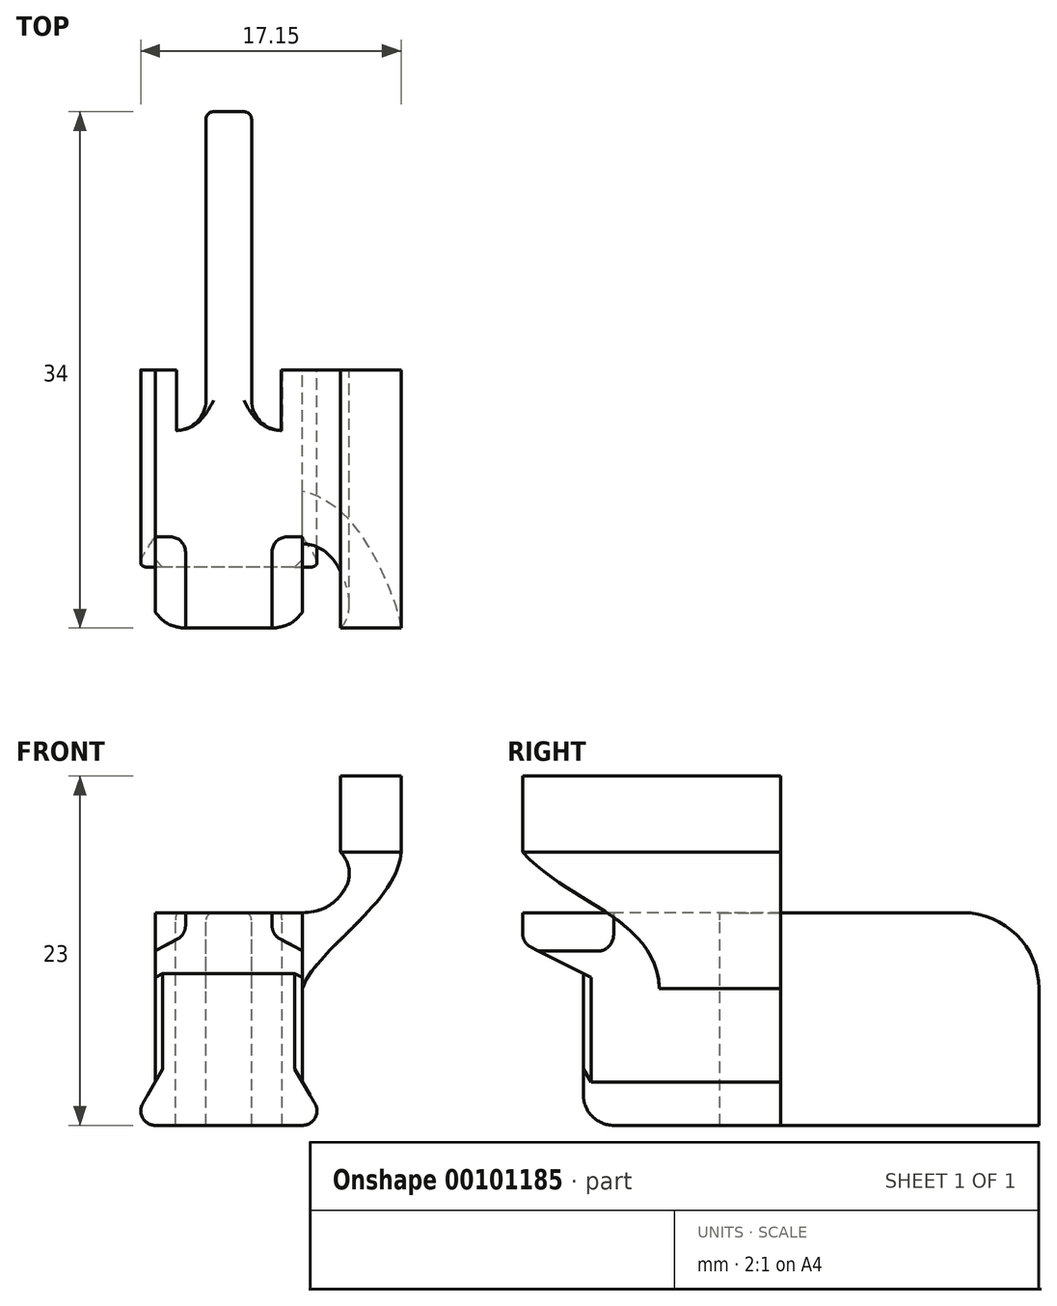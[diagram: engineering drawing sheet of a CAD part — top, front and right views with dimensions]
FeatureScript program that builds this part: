
annotation { "Feature Type Name" : "Feature", "Feature Type Description" : "" }
export const myFeature = defineFeature(function(context is Context, id is Id, definition is map)
    precondition{}
    {
        {
            var Q0;
            Q0=qCreatedBy(makeId("Top.planeOp"),FACE);
            var sketch = newSketch(context, id + "F0", { "sketchPlane" : qUnion([Q0])});
            skLineSegment(sketch, "E0.bottom", {"start": v(4.85, 4.5) * mm, "end": v(-4.85, 4.5) * mm});
            skLineSegment(sketch, "E0.top", {"start": v(4.85, -4.5) * mm, "end": v(-4.85, -4.5) * mm});
            skLineSegment(sketch, "E0.left", {"start": v(4.85, 4.5) * mm, "end": v(4.85, -4.5) * mm});
            skLineSegment(sketch, "E0.right", {"start": v(-4.85, 4.5) * mm, "end": v(-4.85, -4.5) * mm});
            skPoint(sketch, "E0.middle", {"position": v(0, 0) * mm});
            skSolve(sketch);
        }
        {
            var Q0;
            Q0 = qSketchRegion(id + "F0", true);
            extrude(context, id + "F1", {"entities" : qUnion([Q0]), "depth" : 10 * mm});
        }
        {
            var Q0;
            {var subQ0=sQuery(id+"F5.wireOp",EDGE,"E6.right");var subQ1=sQuery(id+"F0.wireOp",EDGE,"E0.bottom");Q0=makeQuery(id+"F8.boolean.opBoolean","MERGE",FACE,{"derivedFrom":[makeQuery(id+"F6.boolean.opBoolean","MERGE",FACE,{"derivedFrom":[makeQuery(id+"F1.opExtrude","SWEPT_FACE",FACE,{"disambiguationData":[OSD([subQ1])]}),makeQuery(id+"F6.opExtrude","SWEPT_FACE",FACE,{"disambiguationData":[OSD([subQ0])]})]}),makeQuery(id+"F8.opExtrude","CAP_FACE",FACE,{"disambiguationData":[OSD([subQ1,sQuery(id+"F0.wireOp",EDGE,"E0.left"),subQ0,sQuery(id+"F7.wireOp",EDGE,"E10.bottom"),sQuery(id+"F7.wireOp",EDGE,"E10.left"),sQuery(id+"F7.wireOp",EDGE,"E10.right"),sQuery(id+"F7.wireOp",EDGE,"E11"),sQuery(id+"F7.wireOp",EDGE,"E12"),sQuery(id+"F7.wireOp",EDGE,"E13.bottom"),sQuery(id+"F7.wireOp",EDGE,"E13.right"),sQuery(id+"F7.wireOp",EDGE,"lhwnHaxV-OdRf-uXD5-QTkz-yTmSrOFCT4aj")])],"isStart":true})]});}
            var sketch = newSketch(context, id + "F2", { "sketchPlane" : qUnion([Q0])});
            skCircle(sketch, "E1", {"center": v(-4.85, 0.95) * mm, "radius": 0.95 * mm});
            skLineSegment(sketch, "E2", {"start": v(-4.85, 2.85) * mm, "end": v(-5.67, 1.42) * mm});
            skLineSegment(sketch, "E3", {"start": v(0, 0) * mm, "end": v(0, 3.09) * mm, "construction": true});
            skCircle(sketch, "E4", {"center": v(4.85, 0.95) * mm, "radius": 0.95 * mm});
            skLineSegment(sketch, "E5", {"start": v(4.85, 2.85) * mm, "end": v(5.67, 1.43) * mm});
            skSolve(sketch);
        }
        {
            var Q0;
            Q0 = qSketchRegion(id + "F2", true);
            var Q1;
            {var subQ0=sQuery(id+"F2.wireOp",EDGE,"E2");Q1=makeQuery(id+"F2.imprint","IMPRINT",FACE,{"disambiguationData":[TD([[makeQuery(id+"F2.imprint","IMPRINT",EDGE,{"derivedFrom":subQ0}),1.0]])]});}
            var Q2;
            {var subQ0=sQuery(id+"F2.wireOp",EDGE,"E5");Q2=makeQuery(id+"F2.imprint","IMPRINT",FACE,{"disambiguationData":[TD([[makeQuery(id+"F2.imprint","IMPRINT",EDGE,{"derivedFrom":subQ0}),-1.0]])]});}
            var Q3;
            Q3=makeQuery(id+"F1.opExtrude","SWEPT_FACE",FACE,{"disambiguationData":[OSD([sQuery(id+"F0.wireOp",EDGE,"E0.top")])]});
            extrude(context, id + "F3", {"entities" : qUnion([Q0, Q1, Q2]), "operationType" : NewBodyOperationType.ADD, "endBound" : BoundingType.UP_TO_SURFACE, "oppositeDirection" : true, "endBoundEntityFace" : qUnion([Q3]), "depth" : 25 * mm});
        }
        {
            var Q0;
            Q0=makeQuery(id+"F1.opExtrude","CAP_EDGE",EDGE,{"disambiguationData":[OSD([sQuery(id+"F0.wireOp",EDGE,"E0.top")])],"isStart":true});
            fillet(context, id + "F4", {"entities" : qUnion([Q0]), "radius" : 2 * mm, "allowEdgeOverflow" : false});
        }
        {
            var Q0;
            Q0=makeQuery(id+"F1.opExtrude","SWEPT_FACE",FACE,{"disambiguationData":[OSD([sQuery(id+"F0.wireOp",EDGE,"E0.left")])]});
            var sketch = newSketch(context, id + "F5", { "sketchPlane" : qUnion([Q0])});
            skLineSegment(sketch, "E6.bottom", {"start": v(-4.5, 10) * mm, "end": v(4.5, 10) * mm});
            skLineSegment(sketch, "E6.top", {"start": v(-4.5, 14) * mm, "end": v(4.5, 14) * mm});
            skLineSegment(sketch, "E6.left", {"start": v(-4.5, 10) * mm, "end": v(-4.5, 14) * mm});
            skLineSegment(sketch, "E6.right", {"start": v(4.5, 10) * mm, "end": v(4.5, 14) * mm});
            skLineSegment(sketch, "E7", {"start": v(-4.5, 14) * mm, "end": v(-8.5, 14) * mm});
            skLineSegment(sketch, "E8", {"start": v(-8.5, 14) * mm, "end": v(-8.5, 12) * mm});
            skLineSegment(sketch, "E9", {"start": v(-8.5, 12) * mm, "end": v(-4.5, 10) * mm});
            skSolve(sketch);
        }
        {
            var Q0;
            Q0 = qSketchRegion(id + "F5", true);
            var Q1;
            Q1=makeQuery(id+"F1.opExtrude","SWEPT_FACE",FACE,{"disambiguationData":[OSD([sQuery(id+"F0.wireOp",EDGE,"E0.right")])]});
            extrude(context, id + "F6", {"entities" : qUnion([Q0]), "operationType" : NewBodyOperationType.ADD, "endBound" : BoundingType.UP_TO_SURFACE, "oppositeDirection" : true, "endBoundEntityFace" : qUnion([Q1]), "offsetDistance" : 25 * mm, "depth" : 25 * mm});
        }
        {
            var Q0;
            {var subQ0=sQuery(id+"F0.wireOp",EDGE,"E0.bottom");Q0=makeQuery(id+"F6.boolean.opBoolean","MERGE",FACE,{"derivedFrom":[makeQuery(id+"F3.boolean.opBoolean","MERGE",FACE,{"derivedFrom":[makeQuery(id+"F1.opExtrude","SWEPT_FACE",FACE,{"disambiguationData":[OSD([subQ0])]}),makeQuery(id+"F3.opExtrude","CAP_FACE",FACE,{"disambiguationData":[OSD([subQ0,sQuery(id+"F0.wireOp",EDGE,"E0.left"),sQuery(id+"F2.wireOp",EDGE,"E1"),sQuery(id+"F2.wireOp",EDGE,"E2")])],"isStart":true}),makeQuery(id+"F3.opExtrude","CAP_FACE",FACE,{"disambiguationData":[OSD([subQ0,sQuery(id+"F0.wireOp",EDGE,"E0.right"),sQuery(id+"F2.wireOp",EDGE,"E4"),sQuery(id+"F2.wireOp",EDGE,"E5")])],"isStart":true})]}),makeQuery(id+"F6.opExtrude","SWEPT_FACE",FACE,{"disambiguationData":[OSD([sQuery(id+"F5.wireOp",EDGE,"E6.right")])]})]});}
            var sketch = newSketch(context, id + "F7", { "sketchPlane" : qUnion([Q0])});
            skLineSegment(sketch, "E10.bottom", {"start": v(-8.35, 23) * mm, "end": v(-11.35, 23) * mm});
            skLineSegment(sketch, "E10.right", {"start": v(-11.35, 23) * mm, "end": v(-11.35, 18) * mm});
            skFitSpline(sketch, "E11", {"points": [v(-8.35, 18) * mm, v(-4.85, 14) * mm], "startDerivative": vector(0.6, -7.03) * mm, "endDerivative": vector(6.53, -0.05) * mm});
            skFitSpline(sketch, "E12", {"points": [v(-11.35, 18) * mm, v(-4.85, 9) * mm], "startDerivative": vector(0.57, -10.14) * mm, "endDerivative": vector(2.5, -7.8) * mm});
            skLineSegment(sketch, "E13.bottom", {"start": v(-8.35, 23) * mm, "end": v(-7.35, 23) * mm});
            skLineSegment(sketch, "E13.top", {"start": v(-8.35, 18) * mm, "end": v(-7.35, 18) * mm});
            skLineSegment(sketch, "E13.right", {"start": v(-7.35, 23) * mm, "end": v(-7.35, 18) * mm});
            skLineSegment(sketch, "E14", {"start": v(-4.85, 9) * mm, "end": v(-4.85, 14) * mm});
            skSolve(sketch);
        }
        {
            var Q0;
            Q0 = qSketchRegion(id + "F7", true);
            var Q1;
            Q1=makeQuery(id+"F6.opExtrude","SWEPT_FACE",FACE,{"disambiguationData":[OSD([sQuery(id+"F5.wireOp",EDGE,"E8")])]});
            extrude(context, id + "F8", {"entities" : qUnion([Q0]), "operationType" : NewBodyOperationType.ADD, "endBound" : BoundingType.UP_TO_SURFACE, "oppositeDirection" : true, "endBoundEntityFace" : qUnion([Q1]), "offsetDistance" : 25 * mm, "depth" : 25 * mm});
        }
        {
            var Q0;
            Q0=makeQuery(id+"F8.opExtrude","SWEPT_FACE",FACE,{"disambiguationData":[OSD([sQuery(id+"F7.wireOp",EDGE,"E10.right")])]});
            var sketch = newSketch(context, id + "F9", { "sketchPlane" : qUnion([Q0])});
            skFitSpline(sketch, "E15", {"points": [v(-8.5, 18) * mm, v(0.5, 9) * mm], "startDerivative": vector(8.93, -10.15) * mm, "endDerivative": vector(0.55, -14.12) * mm});
            skLineSegment(sketch, "E16", {"start": v(-8.5, 18) * mm, "end": v(-8.86, 18) * mm});
            skLineSegment(sketch, "E17", {"start": v(-8.86, 18) * mm, "end": v(-8.86, 9) * mm});
            skLineSegment(sketch, "E18", {"start": v(-8.86, 9) * mm, "end": v(0.5, 9) * mm});
            skSolve(sketch);
        }
        {
            var Q0;
            Q0 = qSketchRegion(id + "F9", true);
            var Q1;
            Q1=makeQuery(id+"F6.boolean.opBoolean","MERGE",FACE,{"derivedFrom":[makeQuery(id+"F1.opExtrude","SWEPT_FACE",FACE,{"disambiguationData":[OSD([sQuery(id+"F0.wireOp",EDGE,"E0.left")])]}),makeQuery(id+"F6.opExtrude","CAP_FACE",FACE,{"disambiguationData":[OSD([sQuery(id+"F5.wireOp",EDGE,"E6.bottom"),sQuery(id+"F5.wireOp",EDGE,"E6.top"),sQuery(id+"F5.wireOp",EDGE,"E6.right"),sQuery(id+"F5.wireOp",EDGE,"E7"),sQuery(id+"F5.wireOp",EDGE,"E8"),sQuery(id+"F5.wireOp",EDGE,"E9")])],"isStart":true})]});
            extrude(context, id + "F10", {"entities" : qUnion([Q0]), "operationType" : NewBodyOperationType.REMOVE, "endBound" : BoundingType.UP_TO_SURFACE, "oppositeDirection" : true, "endBoundEntityFace" : qUnion([Q1]), "depth" : 25 * mm});
        }
        {
            var Q0;
            Q0=qCreatedBy(makeId("Right.planeOp"),FACE);
            var sketch = newSketch(context, id + "F11", { "sketchPlane" : qUnion([Q0])});
            skLineSegment(sketch, "E19.bottom", {"start": v(3.5, 0) * mm, "end": v(25.5, 0) * mm});
            skLineSegment(sketch, "E19.top", {"start": v(3.5, 14) * mm, "end": v(25.5, 14) * mm});
            skLineSegment(sketch, "E19.left", {"start": v(3.5, 0) * mm, "end": v(3.5, 14) * mm});
            skLineSegment(sketch, "E19.right", {"start": v(25.5, 0) * mm, "end": v(25.5, 14) * mm});
            skSolve(sketch);
        }
        {
            var Q0;
            Q0 = qSketchRegion(id + "F11", true);
            extrude(context, id + "F12", {"entities" : qUnion([Q0]), "operationType" : NewBodyOperationType.ADD, "endBound" : BoundingType.SYMMETRIC, "depth" : 3 * mm});
        }
        {
            var Q0;
            Q0=makeQuery(id+"F12.opExtrude","SWEPT_EDGE",EDGE,{"disambiguationData":[OSD([sQuery(id+"F11.wireOp",EDGE,"E19.top"),sQuery(id+"F11.wireOp",EDGE,"E19.right")])]});
            fillet(context, id + "F13", {"entities" : qUnion([Q0]), "radius" : 5 * mm, "tangentPropagation" : true, "allowEdgeOverflow" : false});
        }
        {
            var Q0;
            Q0=makeQuery(id+"F1.opExtrude","SWEPT_EDGE",EDGE,{"disambiguationData":[OSD([sQuery(id+"F0.wireOp",EDGE,"E0.top"),sQuery(id+"F0.wireOp",EDGE,"E0.left")])]});
            var Q1;
            Q1=makeQuery(id+"F1.opExtrude","SWEPT_EDGE",EDGE,{"disambiguationData":[OSD([sQuery(id+"F0.wireOp",EDGE,"E0.top"),sQuery(id+"F0.wireOp",EDGE,"E0.right")])]});
            chamfer(context, id + "F14", {"entities" : qUnion([Q0, Q1]), "width" : 0.5 * mm});
        }
        {
            var Q0;
            {var subQ0=sQuery(id+"F11.wireOp",EDGE,"E19.right");var subQ1=sQuery(id+"F11.wireOp",EDGE,"E19.top");Q0=makeQuery(id+"F13.opFillet","BLEND_EDGE",EDGE,{"blendedFrom":[makeQuery(id+"F12.opExtrude","SWEPT_EDGE",EDGE,{"disambiguationData":[OSD([subQ1,subQ0])]}),makeQuery(id+"F12.opExtrude","CAP_FACE",FACE,{"disambiguationData":[OSD([sQuery(id+"F11.wireOp",EDGE,"E19.bottom"),subQ1,sQuery(id+"F11.wireOp",EDGE,"E19.left"),subQ0])],"isStart":false})],"blendedInto":[makeQuery(id+"F12.opExtrude","CAP_FACE",FACE,{"disambiguationData":[OSD([sQuery(id+"F11.wireOp",EDGE,"E19.bottom"),subQ1,sQuery(id+"F11.wireOp",EDGE,"E19.left"),subQ0])],"isStart":false})]});}
            var Q1;
            {var subQ0=sQuery(id+"F11.wireOp",EDGE,"E19.right");var subQ1=sQuery(id+"F11.wireOp",EDGE,"E19.top");Q1=makeQuery(id+"F13.opFillet","BLEND_EDGE",EDGE,{"blendedFrom":[makeQuery(id+"F12.opExtrude","SWEPT_EDGE",EDGE,{"disambiguationData":[OSD([subQ1,subQ0])]}),makeQuery(id+"F12.opExtrude","CAP_FACE",FACE,{"disambiguationData":[OSD([sQuery(id+"F11.wireOp",EDGE,"E19.bottom"),subQ1,sQuery(id+"F11.wireOp",EDGE,"E19.left"),subQ0])],"isStart":true})],"blendedInto":[makeQuery(id+"F12.opExtrude","CAP_FACE",FACE,{"disambiguationData":[OSD([sQuery(id+"F11.wireOp",EDGE,"E19.bottom"),subQ1,sQuery(id+"F11.wireOp",EDGE,"E19.left"),subQ0])],"isStart":true})]});}
            fillet(context, id + "F15", {"entities" : qUnion([Q0, Q1]), "radius" : 0.5 * mm, "tangentPropagation" : true, "allowEdgeOverflow" : false});
        }
        {
            var Q0;
            Q0=makeQuery(id+"F12.opExtrude","CAP_FACE",FACE,{"disambiguationData":[OSD([sQuery(id+"F11.wireOp",EDGE,"E19.bottom"),sQuery(id+"F11.wireOp",EDGE,"E19.top"),sQuery(id+"F11.wireOp",EDGE,"E19.left"),sQuery(id+"F11.wireOp",EDGE,"E19.right")])],"isStart":false});
            var sketch = newSketch(context, id + "F16", { "sketchPlane" : qUnion([Q0])});
            skText(sketch, "E20", { "text": "Renishaw", "fontName": "OpenSans-Bold.ttf"});
            const initialGuessF16  = {"E20": [0.00663, 0.00758, 1, 0, 0.00224]};
            skSetInitialGuess(sketch, initialGuessF16);
            skSolve(sketch);
        }
        {
            var Q0;
            {var subQ2=sQuery(id+"F5.wireOp",EDGE,"E8");var subQ7=sQuery(id+"F0.wireOp",EDGE,"E0.left");Q0=makeQuery(id+"F10.boolean.opBoolean","SPLIT",FACE,{"disambiguationData":[TD([makeQuery(id+"F1.opExtrude","SWEPT_FACE",FACE,{"disambiguationData":[OSD([subQ7])]})])],"derivedFrom":makeQuery(id+"F8.boolean.opBoolean","MERGE",FACE,{"derivedFrom":[makeQuery(id+"F6.opExtrude","SWEPT_FACE",FACE,{"disambiguationData":[OSD([subQ2])]}),makeQuery(id+"F8.opExtrude","CAP_FACE",FACE,{"disambiguationData":[OSD([subQ2])],"isStart":false})]})});}
            var sketch = newSketch(context, id + "F17", { "sketchPlane" : qUnion([Q0])});
            skLineSegment(sketch, "E21", {"start": v(-4.85, 14) * mm, "end": v(-2.85, 14) * mm});
            skLineSegment(sketch, "E22", {"start": v(-2.85, 14) * mm, "end": v(-2.85, 12.54) * mm});
            skLineSegment(sketch, "E23", {"start": v(-2.85, 12.54) * mm, "end": v(-4.85, 11.48) * mm});
            skLineSegment(sketch, "E24", {"start": v(-4.85, 11.48) * mm, "end": v(-4.85, 14) * mm});
            skLineSegment(sketch, "E25.MirrorCS", {"start": v(2.85, 14) * mm, "end": v(2.85, 12.54) * mm});
            skLineSegment(sketch, "E26.MirrorCS", {"start": v(4.85, 14) * mm, "end": v(2.85, 14) * mm});
            skLineSegment(sketch, "E27.MirrorCS", {"start": v(4.85, 11.48) * mm, "end": v(4.85, 14) * mm});
            skLineSegment(sketch, "E28.MirrorCS", {"start": v(2.85, 12.54) * mm, "end": v(4.85, 11.48) * mm});
            skSolve(sketch);
        }
        {
            var Q0;
            Q0 = qSketchRegion(id + "F17", true);
            extrude(context, id + "F18", {"entities" : qUnion([Q0]), "operationType" : NewBodyOperationType.REMOVE, "oppositeDirection" : true, "depth" : 6 * mm, "offsetDistance" : 25 * mm});
        }
        {
            var Q0;
            Q0=makeQuery(id+"F18.boolean.opBoolean","COPY",EDGE,{"derivedFrom":makeQuery(id+"F18.opExtrude","SWEPT_EDGE",EDGE,{"disambiguationData":[OSD([sQuery(id+"F17.wireOp",EDGE,"E25.MirrorCS"),sQuery(id+"F17.wireOp",EDGE,"E28.MirrorCS")])]})});
            var Q1;
            Q1=makeQuery(id+"F18.boolean.opBoolean","COPY",EDGE,{"derivedFrom":makeQuery(id+"F18.opExtrude","SWEPT_EDGE",EDGE,{"disambiguationData":[OSD([sQuery(id+"F17.wireOp",EDGE,"E22"),sQuery(id+"F17.wireOp",EDGE,"E23")])]})});
            fillet(context, id + "F19", {"entities" : qUnion([Q0, Q1]), "tangentPropagation" : true, "radius" : 1 * mm, "defaultsChanged" : true, "vertexSettings" : [], "allowEdgeOverflow" : false});
        }
        {
            var Q0;
            Q0=makeQuery(id+"F8.opExtrude","SWEPT_EDGE",EDGE,{"disambiguationData":[OSD([sQuery(id+"F7.wireOp",EDGE,"E11"),sQuery(id+"F7.wireOp",EDGE,"E13.top")])]});
            fillet(context, id + "F20", {"entities" : qUnion([Q0]), "tangentPropagation" : true, "radius" : 2 * mm, "defaultsChanged" : true, "vertexSettings" : [], "allowEdgeOverflow" : false});
        }
        {
            var Q0;
            Q0=makeQuery(id+"F18.boolean.opBoolean","COPY",EDGE,{"derivedFrom":makeQuery(id+"F18.opExtrude","CAP_EDGE",EDGE,{"disambiguationData":[OSD([sQuery(id+"F17.wireOp",EDGE,"E22")])],"isStart":false})});
            var Q1;
            Q1=makeQuery(id+"F18.boolean.opBoolean","COPY",EDGE,{"derivedFrom":makeQuery(id+"F18.opExtrude","CAP_EDGE",EDGE,{"disambiguationData":[OSD([sQuery(id+"F17.wireOp",EDGE,"E25.MirrorCS")])],"isStart":false})});
            fillet(context, id + "F21", {"entities" : qUnion([Q0, Q1]), "tangentPropagation" : true, "radius" : 1 * mm, "defaultsChanged" : false, "vertexSettings" : [], "allowEdgeOverflow" : false});
        }
        {
            var Q0;
            Q0=makeQuery(id+"F6.opExtrude","TWEAK_EDGE",EDGE,{"derivedFrom":[makeQuery(id+"F1.opExtrude","SWEPT_FACE",FACE,{"disambiguationData":[OSD([sQuery(id+"F0.wireOp",EDGE,"E0.right")])]}),makeQuery(id+"F5.imprint","IMPRINT",EDGE,{"derivedFrom":sQuery(id+"F5.wireOp",EDGE,"E9")})]});
            var Q1;
            Q1=makeQuery(id+"F6.opExtrude","CAP_EDGE",EDGE,{"disambiguationData":[OSD([sQuery(id+"F5.wireOp",EDGE,"E9")])],"isStart":true});
            var Q2;
            Q2=makeQuery(id+"F6.opExtrude","SWEPT_EDGE",EDGE,{"disambiguationData":[OSD([sQuery(id+"F5.wireOp",EDGE,"E8"),sQuery(id+"F5.wireOp",EDGE,"E9")])]});
            fillet(context, id + "F22", {"entities" : qUnion([Q0, Q1, Q2]), "tangentPropagation" : true, "radius" : 1 * mm, "defaultsChanged" : false, "vertexSettings" : [], "allowEdgeOverflow" : false});
        }
        {
            var Q0;
            {var subQ0=sQuery(id+"F0.wireOp",EDGE,"E0.bottom");Q0=makeQuery(id+"F12.boolean.opBoolean","INTERSECT",EDGE,{"derivedFrom":[makeQuery(id+"F8.boolean.opBoolean","MERGE",FACE,{"derivedFrom":[makeQuery(id+"F6.boolean.opBoolean","MERGE",FACE,{"derivedFrom":[makeQuery(id+"F3.boolean.opBoolean","MERGE",FACE,{"derivedFrom":[makeQuery(id+"F1.opExtrude","SWEPT_FACE",FACE,{"disambiguationData":[OSD([subQ0])]}),makeQuery(id+"F3.opExtrude","CAP_FACE",FACE,{"disambiguationData":[OSD([subQ0,sQuery(id+"F0.wireOp",EDGE,"E0.left"),sQuery(id+"F2.wireOp",EDGE,"E1"),sQuery(id+"F2.wireOp",EDGE,"E2")])],"isStart":true}),makeQuery(id+"F3.opExtrude","CAP_FACE",FACE,{"disambiguationData":[OSD([subQ0,sQuery(id+"F0.wireOp",EDGE,"E0.right"),sQuery(id+"F2.wireOp",EDGE,"E4"),sQuery(id+"F2.wireOp",EDGE,"E5")])],"isStart":true})]}),makeQuery(id+"F6.opExtrude","SWEPT_FACE",FACE,{"disambiguationData":[OSD([sQuery(id+"F5.wireOp",EDGE,"E6.right")])]})]}),makeQuery(id+"F8.opExtrude","CAP_FACE",FACE,{"disambiguationData":[OSD([sQuery(id+"F7.wireOp",EDGE,"E10.bottom"),sQuery(id+"F7.wireOp",EDGE,"E10.right"),sQuery(id+"F7.wireOp",EDGE,"E11"),sQuery(id+"F7.wireOp",EDGE,"E12"),sQuery(id+"F7.wireOp",EDGE,"E13.bottom"),sQuery(id+"F7.wireOp",EDGE,"E13.top"),sQuery(id+"F7.wireOp",EDGE,"E13.right"),sQuery(id+"F7.wireOp",EDGE,"E14")])],"isStart":true})]}),makeQuery(id+"F12.opExtrude","CAP_FACE",FACE,{"disambiguationData":[OSD([sQuery(id+"F11.wireOp",EDGE,"E19.bottom"),sQuery(id+"F11.wireOp",EDGE,"E19.top"),sQuery(id+"F11.wireOp",EDGE,"E19.left"),sQuery(id+"F11.wireOp",EDGE,"E19.right")])],"isStart":true})]});}
            var Q1;
            {var subQ0=sQuery(id+"F0.wireOp",EDGE,"E0.bottom");Q1=makeQuery(id+"F12.boolean.opBoolean","INTERSECT",EDGE,{"derivedFrom":[makeQuery(id+"F8.boolean.opBoolean","MERGE",FACE,{"derivedFrom":[makeQuery(id+"F6.boolean.opBoolean","MERGE",FACE,{"derivedFrom":[makeQuery(id+"F3.boolean.opBoolean","MERGE",FACE,{"derivedFrom":[makeQuery(id+"F1.opExtrude","SWEPT_FACE",FACE,{"disambiguationData":[OSD([subQ0])]}),makeQuery(id+"F3.opExtrude","CAP_FACE",FACE,{"disambiguationData":[OSD([subQ0,sQuery(id+"F0.wireOp",EDGE,"E0.left"),sQuery(id+"F2.wireOp",EDGE,"E1"),sQuery(id+"F2.wireOp",EDGE,"E2")])],"isStart":true}),makeQuery(id+"F3.opExtrude","CAP_FACE",FACE,{"disambiguationData":[OSD([subQ0,sQuery(id+"F0.wireOp",EDGE,"E0.right"),sQuery(id+"F2.wireOp",EDGE,"E4"),sQuery(id+"F2.wireOp",EDGE,"E5")])],"isStart":true})]}),makeQuery(id+"F6.opExtrude","SWEPT_FACE",FACE,{"disambiguationData":[OSD([sQuery(id+"F5.wireOp",EDGE,"E6.right")])]})]}),makeQuery(id+"F8.opExtrude","CAP_FACE",FACE,{"disambiguationData":[OSD([sQuery(id+"F7.wireOp",EDGE,"E10.bottom"),sQuery(id+"F7.wireOp",EDGE,"E10.right"),sQuery(id+"F7.wireOp",EDGE,"E11"),sQuery(id+"F7.wireOp",EDGE,"E12"),sQuery(id+"F7.wireOp",EDGE,"E13.bottom"),sQuery(id+"F7.wireOp",EDGE,"E13.top"),sQuery(id+"F7.wireOp",EDGE,"E13.right"),sQuery(id+"F7.wireOp",EDGE,"E14")])],"isStart":true})]}),makeQuery(id+"F12.opExtrude","CAP_FACE",FACE,{"disambiguationData":[OSD([sQuery(id+"F11.wireOp",EDGE,"E19.bottom"),sQuery(id+"F11.wireOp",EDGE,"E19.top"),sQuery(id+"F11.wireOp",EDGE,"E19.left"),sQuery(id+"F11.wireOp",EDGE,"E19.right")])],"isStart":false})]});}
            fillet(context, id + "F23", {"entities" : qUnion([Q0, Q1]), "tangentPropagation" : true, "radius" : 2 * mm, "defaultsChanged" : false, "vertexSettings" : [], "allowEdgeOverflow" : false});
        }
        {
            var Q0;
            {var subQ0=sQuery(id+"F7.wireOp",EDGE,"E10.left");var subQ1=sQuery(id+"F7.wireOp",EDGE,"E10.right");var subQ4=sQuery(id+"F7.wireOp",EDGE,"E13.right");var subQ7=sQuery(id+"F5.wireOp",EDGE,"E6.right");var subQ9=sQuery(id+"F0.wireOp",EDGE,"E0.right");var subQ10=sQuery(id+"F0.wireOp",EDGE,"E0.left");var subQ11=sQuery(id+"F0.wireOp",EDGE,"E0.bottom");var subQ12=sQuery(id+"F7.wireOp",EDGE,"E13.bottom");var subQ13=sQuery(id+"F7.wireOp",EDGE,"E10.bottom");var subQ14=sQuery(id+"F2.wireOp",EDGE,"E1");var subQ15=sQuery(id+"F7.wireOp",EDGE,"E11");var subQ16=sQuery(id+"F2.wireOp",EDGE,"E2");var subQ17=sQuery(id+"F7.wireOp",EDGE,"E12");var subQ18=sQuery(id+"F7.wireOp",EDGE,"lhwnHaxV-OdRf-uXD5-QTkz-yTmSrOFCT4aj");Q0=makeQuery(id+"F12.boolean.opBoolean","SPLIT",FACE,{"disambiguationData":[TD([makeQuery(id+"F1.opExtrude","SWEPT_FACE",FACE,{"disambiguationData":[OSD([subQ10])]})])],"derivedFrom":makeQuery(id+"F8.boolean.opBoolean","MERGE",FACE,{"derivedFrom":[makeQuery(id+"F6.boolean.opBoolean","MERGE",FACE,{"derivedFrom":[makeQuery(id+"F3.boolean.opBoolean","MERGE",FACE,{"derivedFrom":[makeQuery(id+"F1.opExtrude","SWEPT_FACE",FACE,{"disambiguationData":[OSD([subQ11])]}),makeQuery(id+"F3.opExtrude","CAP_FACE",FACE,{"disambiguationData":[OSD([subQ11,subQ10,subQ14,subQ16])],"isStart":true}),makeQuery(id+"F3.opExtrude","CAP_FACE",FACE,{"disambiguationData":[OSD([subQ11,subQ9,sQuery(id+"F2.wireOp",EDGE,"E4"),sQuery(id+"F2.wireOp",EDGE,"E5")])],"isStart":true})]}),makeQuery(id+"F6.opExtrude","SWEPT_FACE",FACE,{"disambiguationData":[OSD([subQ7])]})]}),makeQuery(id+"F8.opExtrude","CAP_FACE",FACE,{"disambiguationData":[OSD([subQ11,subQ10,subQ7,subQ13,subQ0,subQ1,subQ15,subQ17,subQ12,subQ4,subQ18])],"isStart":true})]})});}
            var Q1;
            {var subQ0=sQuery(id+"F2.wireOp",EDGE,"E5");var subQ1=sQuery(id+"F0.wireOp",EDGE,"E0.right");var subQ2=sQuery(id+"F0.wireOp",EDGE,"E0.left");var subQ3=sQuery(id+"F0.wireOp",EDGE,"E0.bottom");var subQ4=sQuery(id+"F2.wireOp",EDGE,"E4");var subQ7=sQuery(id+"F5.wireOp",EDGE,"E6.right");Q1=makeQuery(id+"F12.boolean.opBoolean","SPLIT",FACE,{"disambiguationData":[TD([makeQuery(id+"F1.opExtrude","SWEPT_FACE",FACE,{"disambiguationData":[OSD([subQ1])]})])],"derivedFrom":makeQuery(id+"F8.boolean.opBoolean","MERGE",FACE,{"derivedFrom":[makeQuery(id+"F6.boolean.opBoolean","MERGE",FACE,{"derivedFrom":[makeQuery(id+"F3.boolean.opBoolean","MERGE",FACE,{"derivedFrom":[makeQuery(id+"F1.opExtrude","SWEPT_FACE",FACE,{"disambiguationData":[OSD([subQ3])]}),makeQuery(id+"F3.opExtrude","CAP_FACE",FACE,{"disambiguationData":[OSD([subQ3,subQ2,sQuery(id+"F2.wireOp",EDGE,"E1"),sQuery(id+"F2.wireOp",EDGE,"E2")])],"isStart":true}),makeQuery(id+"F3.opExtrude","CAP_FACE",FACE,{"disambiguationData":[OSD([subQ3,subQ1,subQ4,subQ0])],"isStart":true})]}),makeQuery(id+"F6.opExtrude","SWEPT_FACE",FACE,{"disambiguationData":[OSD([subQ7])]})]}),makeQuery(id+"F8.opExtrude","CAP_FACE",FACE,{"disambiguationData":[OSD([subQ3,subQ2,subQ7,sQuery(id+"F7.wireOp",EDGE,"E10.bottom"),sQuery(id+"F7.wireOp",EDGE,"E10.left"),sQuery(id+"F7.wireOp",EDGE,"E10.right"),sQuery(id+"F7.wireOp",EDGE,"E11"),sQuery(id+"F7.wireOp",EDGE,"E12"),sQuery(id+"F7.wireOp",EDGE,"E13.bottom"),sQuery(id+"F7.wireOp",EDGE,"E13.right"),sQuery(id+"F7.wireOp",EDGE,"lhwnHaxV-OdRf-uXD5-QTkz-yTmSrOFCT4aj")])],"isStart":true})]})});}
            extrude(context, id + "F24", {"entities" : qUnion([Q0, Q1]), "operationType" : NewBodyOperationType.ADD, "depth" : 4 * mm});
        }
    });
